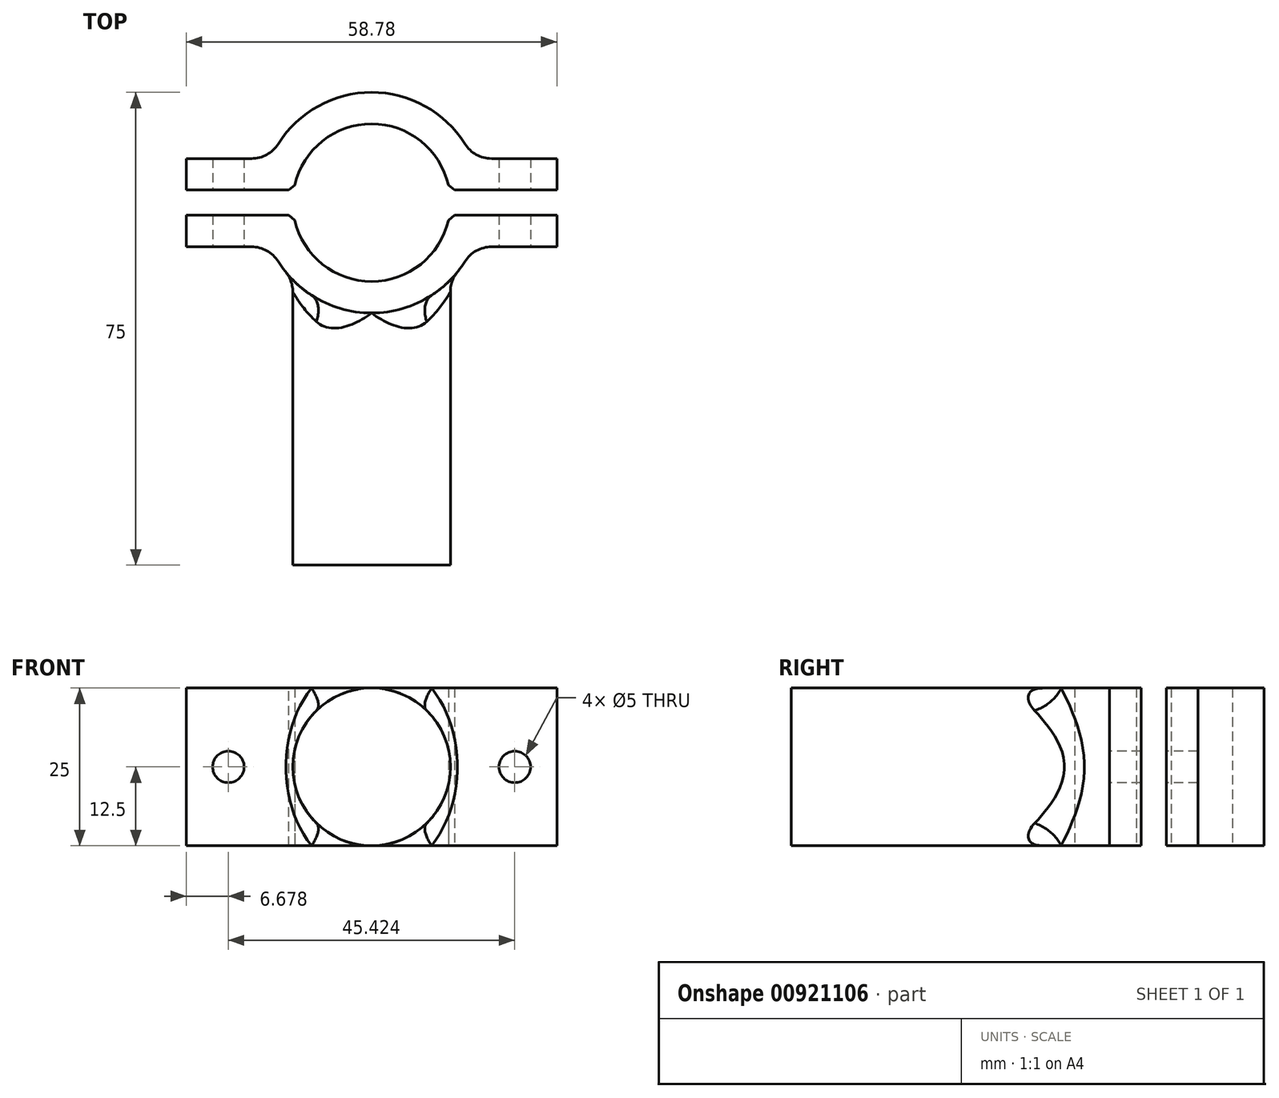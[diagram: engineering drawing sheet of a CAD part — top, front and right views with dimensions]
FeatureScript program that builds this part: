
annotation { "Feature Type Name" : "Feature", "Feature Type Description" : "" }
export const myFeature = defineFeature(function(context is Context, id is Id, definition is map)
    precondition{}
    {
        {
            var Q0;
            Q0=qCreatedBy(makeId("Top.planeOp"),FACE);
            var sketch = newSketch(context, id + "F0", { "sketchPlane" : qUnion([Q0])});
            skArc(sketch, "E0", {"start": v(12.34, 2) * mm, "mid": v(0, 12.5) * mm, "end": v(-12.34, 2) * mm});
            skLineSegment(sketch, "E1", {"start": v(-12.5, 57.5) * mm, "end": v(-12.5, 12.25) * mm});
            skLineSegment(sketch, "E2.MirrorCS", {"start": v(12.5, 57.5) * mm, "end": v(12.5, 12.25) * mm});
            skLineSegment(sketch, "E3", {"start": v(-29.39, 7) * mm, "end": v(-16.04, 7) * mm});
            skLineSegment(sketch, "E4", {"start": v(-29.39, 2) * mm, "end": v(-12.34, 2) * mm});
            skLineSegment(sketch, "E5", {"start": v(-29.39, 7) * mm, "end": v(-29.39, 2) * mm});
            skPoint(sketch, "E6.orphan", {"position": v(-17.39, 2) * mm});
            skPoint(sketch, "E7", {"position": v(-22.71, 2) * mm});
            skPoint(sketch, "E7.positionSnap0", {"position": v(-22.71, 7) * mm});
            skLineSegment(sketch, "E8", {"start": v(-22.71, 7) * mm, "end": v(-22.71, 2) * mm, "construction": true});
            skLineSegment(sketch, "E9.MirrorCS", {"start": v(29.39, 7) * mm, "end": v(16.04, 7) * mm});
            skLineSegment(sketch, "E10.MirrorCS", {"start": v(22.71, 7) * mm, "end": v(22.71, 2) * mm, "construction": true});
            skLineSegment(sketch, "E11.MirrorCS", {"start": v(29.39, 7) * mm, "end": v(29.39, 2) * mm});
            skLineSegment(sketch, "E12.MirrorCS", {"start": v(29.39, 2) * mm, "end": v(12.34, 2) * mm});
            skLineSegment(sketch, "E13.MirrorCS", {"start": v(-29.39, -7) * mm, "end": v(-16.04, -7) * mm});
            skLineSegment(sketch, "E14.MirrorCS", {"start": v(-22.71, -7) * mm, "end": v(-22.71, -2) * mm, "construction": true});
            skLineSegment(sketch, "E15.MirrorCS", {"start": v(-29.39, -7) * mm, "end": v(-29.39, -2) * mm});
            skLineSegment(sketch, "E16.MirrorCS", {"start": v(-29.39, -2) * mm, "end": v(-12.34, -2) * mm});
            skLineSegment(sketch, "E17.MirrorCS", {"start": v(29.39, -2) * mm, "end": v(12.34, -2) * mm});
            skLineSegment(sketch, "E18.MirrorCS", {"start": v(29.39, -7) * mm, "end": v(29.39, -2) * mm});
            skLineSegment(sketch, "E19.MirrorCS", {"start": v(29.39, -7) * mm, "end": v(16.04, -7) * mm});
            skLineSegment(sketch, "E20.MirrorCS", {"start": v(22.71, -7) * mm, "end": v(22.71, -2) * mm, "construction": true});
            skArc(sketch, "E21.trimOffspring", {"start": v(16.04, 7) * mm, "mid": v(0, 17.5) * mm, "end": v(-16.04, 7) * mm});
            skArc(sketch, "E22.trimOffspring", {"start": v(-16.04, -7) * mm, "mid": v(0, -17.5) * mm, "end": v(16.04, -7) * mm});
            skArc(sketch, "E23.trimOffspring", {"start": v(-12.34, -2) * mm, "mid": v(0, -12.5) * mm, "end": v(12.34, -2) * mm});
            skPoint(sketch, "E24", {"position": v(0, 17.5) * mm});
            skSolve(sketch);
        }
        {
            var Q0;
            Q0=makeQuery(id+"F0.imprint","IMPRINT",FACE,{"disambiguationData":[TD([[makeQuery(id+"F0.imprint","IMPRINT",EDGE,{"derivedFrom":sQuery(id+"F0.wireOp",EDGE,"E0")}),-1.0]])]});
            var Q1;
            Q1=makeQuery(id+"F0.imprint","IMPRINT",FACE,{"disambiguationData":[TD([[makeQuery(id+"F0.imprint","IMPRINT",EDGE,{"derivedFrom":sQuery(id+"F0.wireOp",EDGE,"E13.MirrorCS")}),1.0]])]});
            extrude(context, id + "F1", {"entities" : qUnion([Q0, Q1]), "endBound" : BoundingType.SYMMETRIC, "depth" : 25 * mm, "offsetDistance" : 25 * mm});
        }
        {
            var Q0;
            Q0=qCreatedBy(makeId("Front.planeOp"),FACE);
            cPlane(context, id + "F2", {"entities" : qUnion([Q0]), "cplaneType" : CPlaneType.OFFSET, "offset" : 57.5 * mm, "width" : 150 * mm, "height" : 150 * mm});
        }
        {
            var Q0;
            Q0=qCreatedBy(id+"F2.planeOp",FACE);
            var sketch = newSketch(context, id + "F3", { "sketchPlane" : qUnion([Q0])});
            skCircle(sketch, "E25", {"center": v(0, 0) * mm, "radius": 12.5 * mm});
            skSolve(sketch);
        }
        {
            var Q0;
            Q0 = qSketchRegion(id + "F3", true);
            extrude(context, id + "F4", {"entities" : qUnion([Q0]), "operationType" : NewBodyOperationType.ADD, "endBound" : BoundingType.UP_TO_NEXT, "oppositeDirection" : true, "depth" : 25 * mm, "offsetDistance" : 25 * mm});
        }
        {
            var Q0;
            Q0=makeQuery(id+"F1.opExtrude","SWEPT_FACE",FACE,{"disambiguationData":[OSD([sQuery(id+"F0.wireOp",EDGE,"E13.MirrorCS")])]});
            var sketch = newSketch(context, id + "F5", { "sketchPlane" : qUnion([Q0])});
            skPoint(sketch, "E26.0", {"position": v(-22.71, 0) * mm});
            skPoint(sketch, "E27.0", {"position": v(22.71, 0) * mm});
            skCircle(sketch, "E28", {"center": v(22.71, 0) * mm, "radius": 2.5 * mm});
            skCircle(sketch, "E29", {"center": v(-22.71, 0) * mm, "radius": 2.5 * mm});
            skSolve(sketch);
        }
        {
            var Q0;
            Q0=makeQuery(id+"F5.imprint","IMPRINT",FACE,{"disambiguationData":[TD([[makeQuery(id+"F5.imprint","IMPRINT",EDGE,{"derivedFrom":sQuery(id+"F5.wireOp",EDGE,"E29")}),1.0]])]});
            var Q1;
            Q1=makeQuery(id+"F5.imprint","IMPRINT",FACE,{"disambiguationData":[TD([[makeQuery(id+"F5.imprint","IMPRINT",EDGE,{"derivedFrom":sQuery(id+"F5.wireOp",EDGE,"E28")}),1.0]])]});
            extrude(context, id + "F6", {"entities" : qUnion([Q0, Q1]), "operationType" : NewBodyOperationType.REMOVE, "endBound" : BoundingType.THROUGH_ALL, "oppositeDirection" : true, "depth" : 50 * mm, "offsetDistance" : 25 * mm});
        }
        {
            var Q0;
            Q0=makeQuery(id+"F4.boolean.opBoolean","SPLIT",EDGE,{"disambiguationData":[OD(1.0)],"derivedFrom":makeQuery(id+"F4.opExtrude","CAP_EDGE",EDGE,{"disambiguationData":[OSD([sQuery(id+"F3.wireOp",EDGE,"E25")])],"isStart":false})});
            fillet(context, id + "F7", {"entities" : qUnion([Q0]), "radius" : 5 * mm, "tangentPropagation" : true, "allowEdgeOverflow" : false});
        }
        {
            var Q0;
            Q0=makeQuery(id+"F1.opExtrude","SWEPT_EDGE",EDGE,{"disambiguationData":[OSD([sQuery(id+"F0.wireOp",EDGE,"E19.MirrorCS"),sQuery(id+"F0.wireOp",EDGE,"E22.trimOffspring")])]});
            var Q1;
            Q1=makeQuery(id+"F1.opExtrude","SWEPT_EDGE",EDGE,{"disambiguationData":[OSD([sQuery(id+"F0.wireOp",EDGE,"E13.MirrorCS"),sQuery(id+"F0.wireOp",EDGE,"E22.trimOffspring")])]});
            var Q2;
            Q2=makeQuery(id+"F1.opExtrude","SWEPT_EDGE",EDGE,{"disambiguationData":[OSD([sQuery(id+"F0.wireOp",EDGE,"E9.MirrorCS"),sQuery(id+"F0.wireOp",EDGE,"E21.trimOffspring")])]});
            var Q3;
            Q3=makeQuery(id+"F1.opExtrude","SWEPT_EDGE",EDGE,{"disambiguationData":[OSD([sQuery(id+"F0.wireOp",EDGE,"E3"),sQuery(id+"F0.wireOp",EDGE,"E21.trimOffspring")])]});
            fillet(context, id + "F8", {"entities" : qUnion([Q0, Q1, Q2, Q3]), "radius" : 5 * mm, "tangentPropagation" : true, "allowEdgeOverflow" : false});
        }
        {
            var Q0;
            Q0=makeQuery(id+"F1.opExtrude","SWEPT_EDGE",EDGE,{"disambiguationData":[OSD([sQuery(id+"F0.wireOp",EDGE,"E17.MirrorCS"),sQuery(id+"F0.wireOp",EDGE,"E23.trimOffspring")])]});
            var Q1;
            Q1=makeQuery(id+"F1.opExtrude","SWEPT_EDGE",EDGE,{"disambiguationData":[OSD([sQuery(id+"F0.wireOp",EDGE,"E16.MirrorCS"),sQuery(id+"F0.wireOp",EDGE,"E23.trimOffspring")])]});
            var Q2;
            Q2=makeQuery(id+"F1.opExtrude","SWEPT_EDGE",EDGE,{"disambiguationData":[OSD([sQuery(id+"F0.wireOp",EDGE,"E0"),sQuery(id+"F0.wireOp",EDGE,"E12.MirrorCS")])]});
            var Q3;
            Q3=makeQuery(id+"F1.opExtrude","SWEPT_EDGE",EDGE,{"disambiguationData":[OSD([sQuery(id+"F0.wireOp",EDGE,"E0"),sQuery(id+"F0.wireOp",EDGE,"E4")])]});
            chamfer(context, id + "F9", {"entities" : qUnion([Q0, Q1, Q2, Q3]), "width" : 1 * mm, "tangentPropagation" : true});
        }
    });
